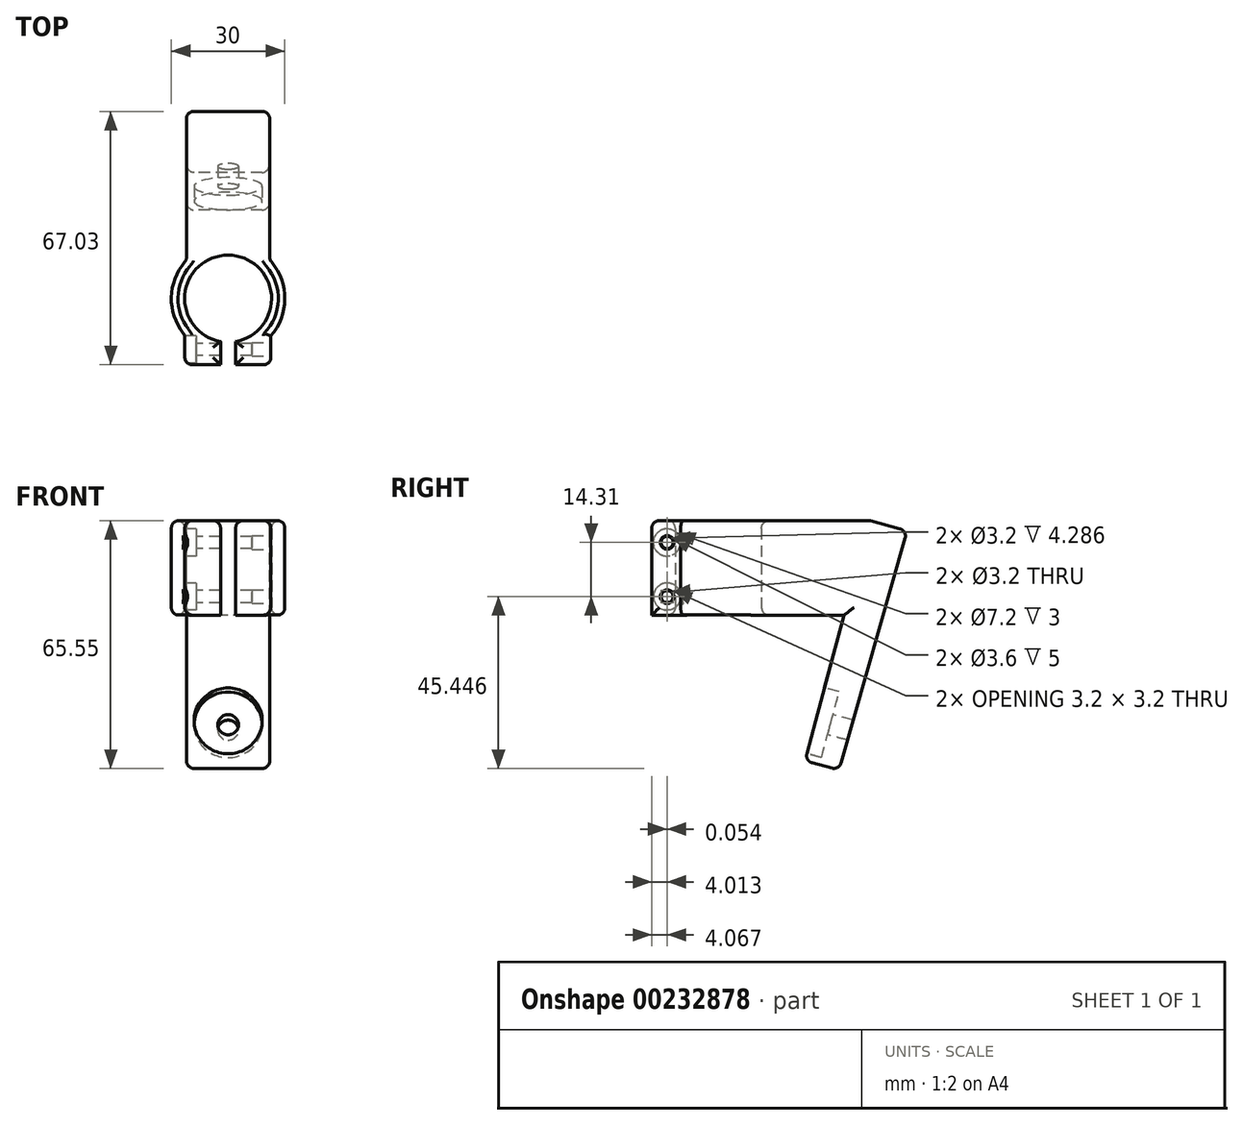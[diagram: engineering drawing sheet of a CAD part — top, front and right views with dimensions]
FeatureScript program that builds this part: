
annotation { "Feature Type Name" : "Feature", "Feature Type Description" : "" }
export const myFeature = defineFeature(function(context is Context, id is Id, definition is map)
    precondition{}
    {
        {
            var Q0;
            Q0=qCreatedBy(makeId("Top.planeOp"),FACE);
            var sketch = newSketch(context, id + "F0", { "sketchPlane" : qUnion([Q0])});
            skCircle(sketch, "E0", {"center": v(0, 0) * mm, "radius": 11.5 * mm});
            skCircle(sketch, "E1", {"center": v(0, 0) * mm, "radius": 15 * mm});
            skLineSegment(sketch, "E2.bottom", {"start": v(-11.45, -17.5) * mm, "end": v(11.29, -17.5) * mm});
            skLineSegment(sketch, "E2.top", {"start": v(-11.45, -9.5) * mm, "end": v(11.29, -9.5) * mm});
            skLineSegment(sketch, "E2.left", {"start": v(-11.45, -17.5) * mm, "end": v(-11.45, -9.5) * mm});
            skLineSegment(sketch, "E2.right", {"start": v(11.29, -17.5) * mm, "end": v(11.29, -9.5) * mm});
            skLineSegment(sketch, "E3.bottom", {"start": v(-11, 40) * mm, "end": v(11, 40) * mm});
            skLineSegment(sketch, "E3.top", {"start": v(-11, 0) * mm, "end": v(11, 0) * mm});
            skLineSegment(sketch, "E3.left", {"start": v(-11, 40) * mm, "end": v(-11, 0) * mm});
            skLineSegment(sketch, "E3.right", {"start": v(11, 40) * mm, "end": v(11, 0) * mm});
            skSolve(sketch);
        }
        {
            var Q0;
            {var subQ5=sQuery(id+"F0.wireOp",EDGE,"E2.bottom");Q0=makeQuery(id+"F0.imprint","IMPRINT",FACE,{"disambiguationData":[TD([[makeQuery(id+"F0.imprint","IMPRINT",EDGE,{"derivedFrom":subQ5}),1.0]])]});}
            var Q1;
            {var subQ5=sQuery(id+"F0.wireOp",EDGE,"E0");var subQ7=sQuery(id+"F0.wireOp",EDGE,"E3.left");var subQ9=makeQuery(id+"F0.imprint","INTERSECT",VERTEX,{"derivedFrom":[subQ5,subQ7]});Q1=makeQuery(id+"F0.imprint","IMPRINT",FACE,{"disambiguationData":[TD([[makeQuery(id+"F0.imprint","IMPRINT",EDGE,{"disambiguationData":[TD([[subQ9,-1.0]])],"derivedFrom":subQ5}),-1.0]])]});}
            var Q2;
            {var subQ1=sQuery(id+"F0.wireOp",EDGE,"E2.top");var subQ3=sQuery(id+"F0.wireOp",EDGE,"E0");var subQ7=makeQuery(id+"F0.imprint","INTERSECT",VERTEX,{"disambiguationData":[OD(0.0)],"derivedFrom":[subQ3,subQ1]});Q2=makeQuery(id+"F0.imprint","IMPRINT",FACE,{"disambiguationData":[TD([[makeQuery(id+"F0.imprint","IMPRINT",EDGE,{"disambiguationData":[TD([[subQ7,-1.0]])],"derivedFrom":subQ3}),-1.0]])]});}
            var Q3;
            {var subQ5=sQuery(id+"F0.wireOp",EDGE,"E0");var subQ7=sQuery(id+"F0.wireOp",EDGE,"E3.right");var subQ9=makeQuery(id+"F0.imprint","INTERSECT",VERTEX,{"derivedFrom":[subQ5,subQ7]});Q3=makeQuery(id+"F0.imprint","IMPRINT",FACE,{"disambiguationData":[TD([[makeQuery(id+"F0.imprint","IMPRINT",EDGE,{"disambiguationData":[TD([[subQ9,1.0]])],"derivedFrom":subQ5}),-1.0]])]});}
            var Q4;
            {var subQ0=sQuery(id+"F0.wireOp",EDGE,"E3.left");var subQ1=sQuery(id+"F0.wireOp",EDGE,"E0");var subQ2=makeQuery(id+"F0.imprint","INTERSECT",VERTEX,{"derivedFrom":[subQ1,subQ0]});Q4=makeQuery(id+"F0.imprint","IMPRINT",FACE,{"disambiguationData":[TD([[makeQuery(id+"F0.imprint","IMPRINT",EDGE,{"disambiguationData":[TD([[subQ2,1.0]])],"derivedFrom":subQ1}),-1.0]])]});}
            var Q5;
            {var subQ5=sQuery(id+"F0.wireOp",EDGE,"E3.bottom");Q5=makeQuery(id+"F0.imprint","IMPRINT",FACE,{"disambiguationData":[TD([[makeQuery(id+"F0.imprint","IMPRINT",EDGE,{"derivedFrom":subQ5}),-1.0]])]});}
            extrude(context, id + "F1", {"entities" : qUnion([Q0, Q1, Q2, Q3, Q4, Q5]), "depth" : 25 * mm});
        }
        {
            var Q0;
            Q0=makeQuery(id+"F1.opExtrude","SWEPT_FACE",FACE,{"disambiguationData":[OSD([sQuery(id+"F0.wireOp",EDGE,"E2.left")])]});
            var sketch = newSketch(context, id + "F2", { "sketchPlane" : qUnion([Q0])});
            skPoint(sketch, "E4.centerSnap0", {"position": v(13.6, 0) * mm});
            skPoint(sketch, "E5", {"position": v(13.44, 4.9) * mm});
            skCircle(sketch, "E6", {"center": v(13.44, 4.9) * mm, "radius": 3.6 * mm});
            skPoint(sketch, "E7", {"position": v(13.44, 19.2) * mm});
            skCircle(sketch, "E8", {"center": v(13.5, 19.2) * mm, "radius": 3.6 * mm});
            skSolve(sketch);
        }
        {
            var Q0;
            Q0=sQuery(id+"F2.wireOp",VERTEX,"E5");
            var Q1;
            Q1=sQuery(id+"F2.wireOp",VERTEX,"E7");
            var Q2;
            Q2=makeQuery(id+"F1.opExtrude","SWEPT_BODY",BODY,{"disambiguationData":[OSD([sQuery(id+"F0.wireOp",EDGE,"E0"),sQuery(id+"F0.wireOp",EDGE,"E1"),sQuery(id+"F0.wireOp",EDGE,"E2.bottom"),sQuery(id+"F0.wireOp",EDGE,"E2.top"),sQuery(id+"F0.wireOp",EDGE,"E2.left"),sQuery(id+"F0.wireOp",EDGE,"E2.right")])]});
            hole(context, id + "F3", {"style" : HoleStyle.SIMPLE, "endStyle" : HoleEndStyle.THROUGH, "holeDiameter" : 3.2 * mm, "locations" : qUnion([Q0, Q1]), "scope" : qUnion([Q2]), "isTappedThrough" : true});
        }
        {
            var Q0;
            Q0=qCreatedBy(makeId("Right.planeOp"),FACE);
            var sketch = newSketch(context, id + "F4", { "sketchPlane" : qUnion([Q0])});
            skLineSegment(sketch, "E9.bottom", {"start": v(0, 29) * mm, "end": v(-29.16, 29) * mm});
            skLineSegment(sketch, "E9.top", {"start": v(0, -1) * mm, "end": v(-29.16, -1) * mm});
            skLineSegment(sketch, "E9.left", {"start": v(0, 29) * mm, "end": v(0, -1) * mm});
            skLineSegment(sketch, "E9.right", {"start": v(-29.16, 29) * mm, "end": v(-29.16, -1) * mm});
            skSolve(sketch);
        }
        {
            var Q0;
            Q0=qSketchRegion(id+"F4",true);
            extrude(context, id + "F5", {"entities" : qUnion([Q0]), "operationType" : NewBodyOperationType.REMOVE, "oppositeDirection" : true, "depth" : 2 * mm, "hasSecondDirection" : true, "secondDirectionOppositeDirection" : false, "secondDirectionDepth" : 2 * mm});
        }
        {
            var Q0;
            Q0=makeQuery(id+"F2.imprint","IMPRINT",FACE,{"disambiguationData":[TD([[makeQuery(id+"F2.imprint","IMPRINT",EDGE,{"derivedFrom":sQuery(id+"F2.wireOp",EDGE,"E6")}),1.0]])]});
            var Q1;
            Q1=makeQuery(id+"F2.imprint","IMPRINT",FACE,{"disambiguationData":[TD([[makeQuery(id+"F2.imprint","IMPRINT",EDGE,{"derivedFrom":sQuery(id+"F2.wireOp",EDGE,"E8")}),1.0]])]});
            var Q2;
            Q2=sQuery(id+"F2.wireOp",EDGE,"E6");
            var Q3;
            Q3=sQuery(id+"F2.wireOp",EDGE,"E8");
            extrude(context, id + "F6", {"entities" : qUnion([Q0, Q1]), "operationType" : NewBodyOperationType.REMOVE, "surfaceEntities" : qUnion([Q2, Q3]), "oppositeDirection" : true, "depth" : 3 * mm});
        }
        {
            var Q0;
            Q0=makeQuery(id+"F1.opExtrude","SWEPT_FACE",FACE,{"disambiguationData":[OSD([sQuery(id+"F0.wireOp",EDGE,"E2.right")])]});
            var sketch = newSketch(context, id + "F7", { "sketchPlane" : qUnion([Q0])});
            skCircle(sketch, "E10", {"center": v(-13.44, 19.2) * mm, "radius": 1.8 * mm});
            skCircle(sketch, "E11", {"center": v(-13.44, 4.9) * mm, "radius": 1.8 * mm});
            skSolve(sketch);
        }
        {
            var Q0;
            Q0=makeQuery(id+"F7.imprint","IMPRINT",FACE,{"disambiguationData":[TD([[makeQuery(id+"F7.imprint","IMPRINT",EDGE,{"derivedFrom":sQuery(id+"F7.wireOp",EDGE,"E10")}),1.0]])]});
            var Q1;
            Q1=makeQuery(id+"F7.imprint","IMPRINT",FACE,{"disambiguationData":[TD([[makeQuery(id+"F7.imprint","IMPRINT",EDGE,{"derivedFrom":sQuery(id+"F7.wireOp",EDGE,"E11")}),1.0]])]});
            var Q2;
            Q2=sQuery(id+"F7.wireOp",EDGE,"E10");
            var Q3;
            Q3=sQuery(id+"F7.wireOp",EDGE,"E11");
            extrude(context, id + "F8", {"entities" : qUnion([Q0, Q1]), "operationType" : NewBodyOperationType.REMOVE, "surfaceEntities" : qUnion([Q2, Q3]), "oppositeDirection" : true, "depth" : 5 * mm});
        }
        {
            var Q0;
            Q0=makeQuery(id+"F1.opExtrude","SWEPT_FACE",FACE,{"disambiguationData":[OSD([sQuery(id+"F0.wireOp",EDGE,"E3.left")])]});
            var sketch = newSketch(context, id + "F9", { "sketchPlane" : qUnion([Q0])});
            skPoint(sketch, "E12.endSnap0", {"position": v(-40, 12.5) * mm});
            skLineSegment(sketch, "E13", {"start": v(-40, 25) * mm, "end": v(-22.96, -38.58) * mm});
            skLineSegment(sketch, "E14", {"start": v(-22.96, -38.58) * mm, "end": v(-31.96, -41) * mm});
            skLineSegment(sketch, "E15", {"start": v(-31.96, -41) * mm, "end": v(-50, 22.32) * mm});
            skLineSegment(sketch, "E16", {"start": v(-50, 22.32) * mm, "end": v(-40, 25) * mm});
            skSolve(sketch);
        }
        {
            var Q0;
            {var subQ0=sQuery(id+"F9.wireOp",EDGE,"E14");Q0=makeQuery(id+"F9.imprint","IMPRINT",FACE,{"disambiguationData":[TD([[makeQuery(id+"F9.imprint","IMPRINT",EDGE,{"derivedFrom":subQ0}),-1.0]])]});}
            var Q1;
            {var subQ1=sQuery(id+"F0.wireOp",EDGE,"E3.left");var subQ2=makeQuery(id+"F1.opExtrude","SWEPT_EDGE",EDGE,{"disambiguationData":[OSD([sQuery(id+"F0.wireOp",EDGE,"E3.bottom"),subQ1])]});Q1=makeQuery(id+"F9.imprint","IMPRINT",FACE,{"disambiguationData":[TD([[makeQuery(id+"F9.imprint","IMPRINT",EDGE,{"derivedFrom":subQ2}),1.0]])]});}
            extrude(context, id + "F10", {"entities" : qUnion([Q0, Q1]), "operationType" : NewBodyOperationType.ADD, "oppositeDirection" : true, "depth" : 22 * mm});
        }
        {
            var Q0;
            Q0=makeQuery(id+"F10.opExtrude","SWEPT_FACE",FACE,{"disambiguationData":[OSD([sQuery(id+"F9.wireOp",EDGE,"E13")])]});
            var sketch = newSketch(context, id + "F11", { "sketchPlane" : qUnion([Q0])});
            skPoint(sketch, "E17", {"position": v(0, -20.32) * mm});
            skSolve(sketch);
        }
        {
            var Q0;
            Q0=sQuery(id+"F11.wireOp",VERTEX,"E17");
            var Q1;
            Q1=makeQuery(id+"F1.opExtrude","SWEPT_BODY",BODY,{"disambiguationData":[OSD([sQuery(id+"F0.wireOp",EDGE,"E0"),sQuery(id+"F0.wireOp",EDGE,"E1"),sQuery(id+"F0.wireOp",EDGE,"E2.bottom"),sQuery(id+"F0.wireOp",EDGE,"E2.left"),sQuery(id+"F0.wireOp",EDGE,"E2.right"),sQuery(id+"F0.wireOp",EDGE,"E3.bottom"),sQuery(id+"F0.wireOp",EDGE,"E3.left"),sQuery(id+"F0.wireOp",EDGE,"E3.right")])]});
            hole(context, id + "F12", {"style" : HoleStyle.C_BORE, "endStyle" : HoleEndStyle.THROUGH, "holeDiameter" : 5.5 * mm, "cBoreDiameter" : 18 * mm, "cBoreDepth" : 4 * mm, "locations" : qUnion([Q0]), "scope" : qUnion([Q1]), "tappedDepth" : 12 * mm, "tapClearance" : 3});
        }
        {
            var Q0;
            Q0=makeQuery(id+"F12.hole-0.boolean.opBoolean","COPY",EDGE,{"derivedFrom":makeQuery(id+"F12.hole-0.opRevolve","SWEPT_EDGE",EDGE,{"disambiguationData":[OSD([sQuery(id+"F12.hole-0.sketch.wireOp",EDGE,"cbore_start_line_2"),sQuery(id+"F12.hole-0.sketch.wireOp",EDGE,"cbore_start_line_3")])]})});
            var Q1;
            Q1=makeQuery(id+"F1.opExtrude","SWEPT_EDGE",EDGE,{"disambiguationData":[OSD([sQuery(id+"F0.wireOp",EDGE,"E2.bottom"),sQuery(id+"F0.wireOp",EDGE,"E2.right")])]});
            var Q2;
            Q2=makeQuery(id+"F1.opExtrude","CAP_EDGE",EDGE,{"disambiguationData":[OSD([sQuery(id+"F0.wireOp",EDGE,"E2.right")])],"isStart":true});
            var Q3;
            Q3=makeQuery(id+"F1.opExtrude","CAP_EDGE",EDGE,{"disambiguationData":[OSD([sQuery(id+"F0.wireOp",EDGE,"E0")])],"isStart":true});
            var Q4;
            Q4=makeQuery(id+"F1.opExtrude","SWEPT_EDGE",EDGE,{"disambiguationData":[OSD([sQuery(id+"F0.wireOp",EDGE,"E2.bottom"),sQuery(id+"F0.wireOp",EDGE,"E2.left")])]});
            var Q5;
            Q5=makeQuery(id+"F1.opExtrude","CAP_EDGE",EDGE,{"disambiguationData":[OSD([sQuery(id+"F0.wireOp",EDGE,"E2.left")])],"isStart":true});
            var Q6;
            Q6=makeQuery(id+"F1.opExtrude","CAP_EDGE",EDGE,{"disambiguationData":[OSD([sQuery(id+"F0.wireOp",EDGE,"E3.right")])],"isStart":true});
            var Q7;
            {var subQ0=sQuery(id+"F0.wireOp",EDGE,"E1");Q7=makeQuery(id+"F1.opExtrude","CAP_EDGE",EDGE,{"disambiguationData":[OSD([subQ0]),TDD([makeQuery(id+"F0.imprint","IMPRINT",EDGE,{"disambiguationData":[TD([[makeQuery(id+"F0.imprint","INTERSECT",VERTEX,{"derivedFrom":[subQ0,sQuery(id+"F0.wireOp",EDGE,"E3.right")]}),1.0]])],"derivedFrom":subQ0})])],"isStart":true});}
            var Q8;
            Q8=makeQuery(id+"F1.opExtrude","CAP_EDGE",EDGE,{"disambiguationData":[OSD([sQuery(id+"F0.wireOp",EDGE,"E3.left")])],"isStart":true});
            var Q9;
            {var subQ0=sQuery(id+"F0.wireOp",EDGE,"E1");Q9=makeQuery(id+"F1.opExtrude","CAP_EDGE",EDGE,{"disambiguationData":[OSD([subQ0]),TDD([makeQuery(id+"F0.imprint","IMPRINT",EDGE,{"disambiguationData":[TD([[makeQuery(id+"F0.imprint","INTERSECT",VERTEX,{"derivedFrom":[subQ0,sQuery(id+"F0.wireOp",EDGE,"E3.left")]}),-1.0]])],"derivedFrom":subQ0})])],"isStart":true});}
            var Q10;
            Q10=makeQuery(id+"F1.opExtrude","SWEPT_EDGE",EDGE,{"disambiguationData":[OSD([sQuery(id+"F0.wireOp",EDGE,"E1"),sQuery(id+"F0.wireOp",EDGE,"E3.left")])]});
            var Q11;
            Q11=makeQuery(id+"F1.opExtrude","SWEPT_EDGE",EDGE,{"disambiguationData":[OSD([sQuery(id+"F0.wireOp",EDGE,"E1"),sQuery(id+"F0.wireOp",EDGE,"E2.left")])]});
            var Q12;
            Q12=makeQuery(id+"F10.opExtrude","CAP_EDGE",EDGE,{"disambiguationData":[OSD([sQuery(id+"F9.wireOp",EDGE,"E16")])],"isStart":true});
            var Q13;
            Q13=makeQuery(id+"F10.opExtrude","CAP_EDGE",EDGE,{"disambiguationData":[OSD([sQuery(id+"F9.wireOp",EDGE,"E16")])],"isStart":false});
            var Q14;
            Q14=makeQuery(id+"F10.opExtrude","SWEPT_FACE",FACE,{"disambiguationData":[OSD([sQuery(id+"F9.wireOp",EDGE,"E16")])]});
            var Q15;
            Q15=makeQuery(id+"F1.opExtrude","CAP_FACE",FACE,{"disambiguationData":[OSD([sQuery(id+"F0.wireOp",EDGE,"E0"),sQuery(id+"F0.wireOp",EDGE,"E1"),sQuery(id+"F0.wireOp",EDGE,"E2.bottom"),sQuery(id+"F0.wireOp",EDGE,"E2.left"),sQuery(id+"F0.wireOp",EDGE,"E2.right"),sQuery(id+"F0.wireOp",EDGE,"E3.bottom"),sQuery(id+"F0.wireOp",EDGE,"E3.left"),sQuery(id+"F0.wireOp",EDGE,"E3.right")])],"isStart":false});
            var Q16;
            Q16=makeQuery(id+"F10.boolean.opBoolean","MERGE",FACE,{"derivedFrom":[makeQuery(id+"F1.opExtrude","SWEPT_FACE",FACE,{"disambiguationData":[OSD([sQuery(id+"F0.wireOp",EDGE,"E3.left")])]}),makeQuery(id+"F10.opExtrude","CAP_FACE",FACE,{"disambiguationData":[OSD([sQuery(id+"F9.wireOp",EDGE,"E13"),sQuery(id+"F9.wireOp",EDGE,"E14"),sQuery(id+"F9.wireOp",EDGE,"E15"),sQuery(id+"F9.wireOp",EDGE,"E16")])],"isStart":true})]});
            var Q17;
            Q17=makeQuery(id+"F10.boolean.opBoolean","MERGE",FACE,{"derivedFrom":[makeQuery(id+"F1.opExtrude","SWEPT_FACE",FACE,{"disambiguationData":[OSD([sQuery(id+"F0.wireOp",EDGE,"E3.right")])]}),makeQuery(id+"F10.opExtrude","CAP_FACE",FACE,{"disambiguationData":[OSD([sQuery(id+"F9.wireOp",EDGE,"E13"),sQuery(id+"F9.wireOp",EDGE,"E14"),sQuery(id+"F9.wireOp",EDGE,"E15"),sQuery(id+"F9.wireOp",EDGE,"E16")])],"isStart":false})]});
            var Q18;
            Q18=makeQuery(id+"F10.opExtrude","SWEPT_EDGE",EDGE,{"disambiguationData":[OSD([sQuery(id+"F9.wireOp",EDGE,"E14"),sQuery(id+"F9.wireOp",EDGE,"E15")])]});
            var Q19;
            Q19=makeQuery(id+"F10.opExtrude","SWEPT_EDGE",EDGE,{"disambiguationData":[OSD([sQuery(id+"F9.wireOp",EDGE,"E13"),sQuery(id+"F9.wireOp",EDGE,"E14")])]});
            var Q20;
            {var subQ0=sQuery(id+"F0.wireOp",EDGE,"E3.bottom");Q20=makeQuery(id+"F10.boolean.opBoolean","MERGE",EDGE,{"derivedFrom":[makeQuery(id+"F1.opExtrude","CAP_EDGE",EDGE,{"disambiguationData":[OSD([subQ0])],"isStart":false}),makeQuery(id+"F10.opExtrude","SWEPT_EDGE",EDGE,{"disambiguationData":[OSD([subQ0,sQuery(id+"F0.wireOp",EDGE,"E3.left"),sQuery(id+"F9.wireOp",EDGE,"E13"),sQuery(id+"F9.wireOp",EDGE,"E16")])]})]});}
            fillet(context, id + "F13", {"entities" : qUnion([Q0, Q1, Q2, Q3, Q4, Q5, Q6, Q7, Q8, Q9, Q10, Q11, Q12, Q13, Q14, Q15, Q16, Q17, Q18, Q19, Q20]), "radius" : 2 * mm, "tangentPropagation" : true, "allowEdgeOverflow" : false});
        }
    });
